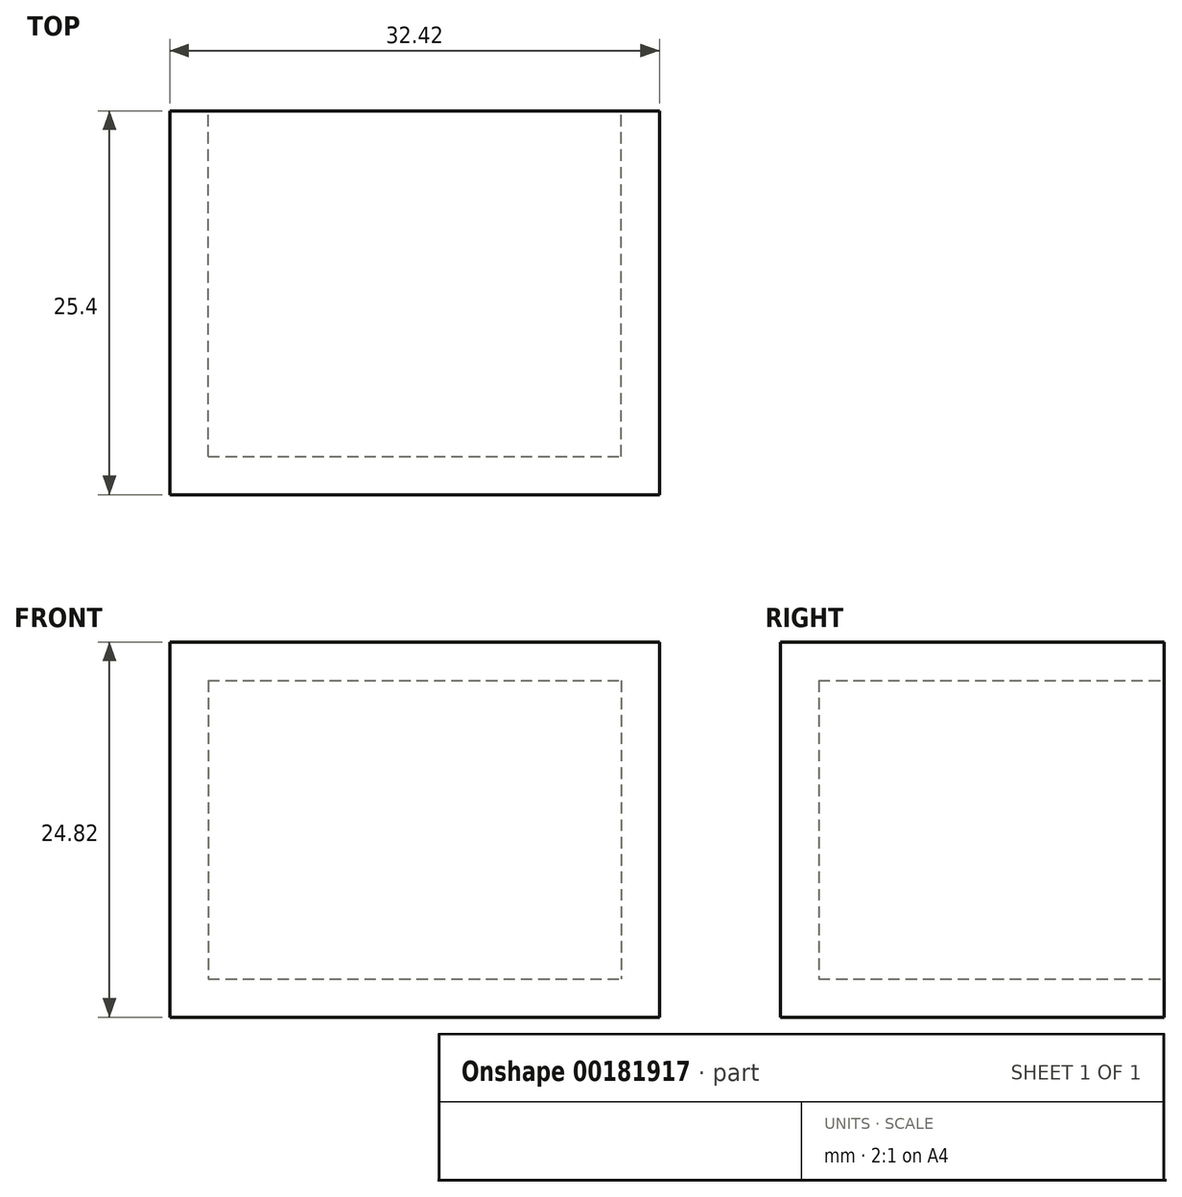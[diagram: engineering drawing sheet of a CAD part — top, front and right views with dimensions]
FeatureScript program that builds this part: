
annotation { "Feature Type Name" : "Feature", "Feature Type Description" : "" }
export const myFeature = defineFeature(function(context is Context, id is Id, definition is map)
    precondition{}
    {
        {
            var Q0;
            Q0=qCreatedBy(makeId("Front.planeOp"),FACE);
            var sketch = newSketch(context, id + "F0", { "sketchPlane" : qUnion([Q0])});
            skLineSegment(sketch, "E0.bottom", {"start": v(-46.14, 38.84) * mm, "end": v(-13.72, 38.84) * mm});
            skLineSegment(sketch, "E0.top", {"start": v(-46.14, 14.02) * mm, "end": v(-13.72, 14.02) * mm});
            skLineSegment(sketch, "E0.left", {"start": v(-46.14, 38.84) * mm, "end": v(-46.14, 14.02) * mm});
            skLineSegment(sketch, "E0.right", {"start": v(-13.72, 38.84) * mm, "end": v(-13.72, 14.02) * mm});
            skSolve(sketch);
        }
        {
            var Q0;
            Q0=makeQuery(id+"F0.imprint","IMPRINT",FACE,{"disambiguationData":[TD([[makeQuery(id+"F0.imprint","IMPRINT",EDGE,{"derivedFrom":sQuery(id+"F0.wireOp",EDGE,"E0.bottom")}),-1.0]])]});
            extrude(context, id + "F1", {"entities" : qUnion([Q0]), "depth" : 25.4 * mm});
        }
        {
            var Q0;
            Q0=makeQuery(id+"F1.opExtrude","CAP_FACE",FACE,{"disambiguationData":[OSD([sQuery(id+"F0.wireOp",EDGE,"E0.bottom"),sQuery(id+"F0.wireOp",EDGE,"E0.top"),sQuery(id+"F0.wireOp",EDGE,"E0.left"),sQuery(id+"F0.wireOp",EDGE,"E0.right")])],"isStart":true});
            shell(context, id + "F2", {"entities" : qUnion([Q0]), "thickness" : 2.54 * mm});
        }
    });
